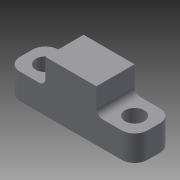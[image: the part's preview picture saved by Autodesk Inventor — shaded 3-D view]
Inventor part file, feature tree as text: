
AUTODESK INVENTOR PART (.ipt)
format: ipt  version: 2015 (Build 190159000, 159)  size: 115,712 bytes
history: native  units: in
note: dims shown in document units (in); Inventor stores cm internally (conversion verified against a paired STEP export)
features: fillet x4, sketch x2, extrude x1, hole x1, mirror x1
ambient origin geometry x8: Origin, YZ Plane, XZ Plane, XY Plane, X Axis, Y Axis, Z Axis, Center Point
bodies: Solid1 (feature_tree)
feature tree (9):
  extrude  "Extrusion1"  Depth=1.25in
  hole  "Hole1"  [1 undecoded]
  fillet  "Fillet1"  Radius=0.75in
  fillet  "Fillet2"  Radius=0.375in
  mirror  "Mirror1"
  fillet  "Fillet3"  Radius=0.375in
  fillet  "Fillet4"  Radius=0.25in
  sketch  "Sketch1"  dims[d0=0.5in d1=1.25in]
  sketch  "Sketch2"  dims[d2=0.75in d3=0.5in d4=0.75in d5=0.0in d6=0.375in d7=0.375in d8=0.375in d9=0.75in d10=0.375in d11=0.25in d12=0.5635in d13=1.0in d14=0.8108in d15=0.25in d16=0.25in d17=0.125in d18=0.125in]
note: 1 required parameter value undecoded (feature->parameter linkage not recoverable at this tier; creation-order binding heuristic only, values carry confidence <= 0.55)
